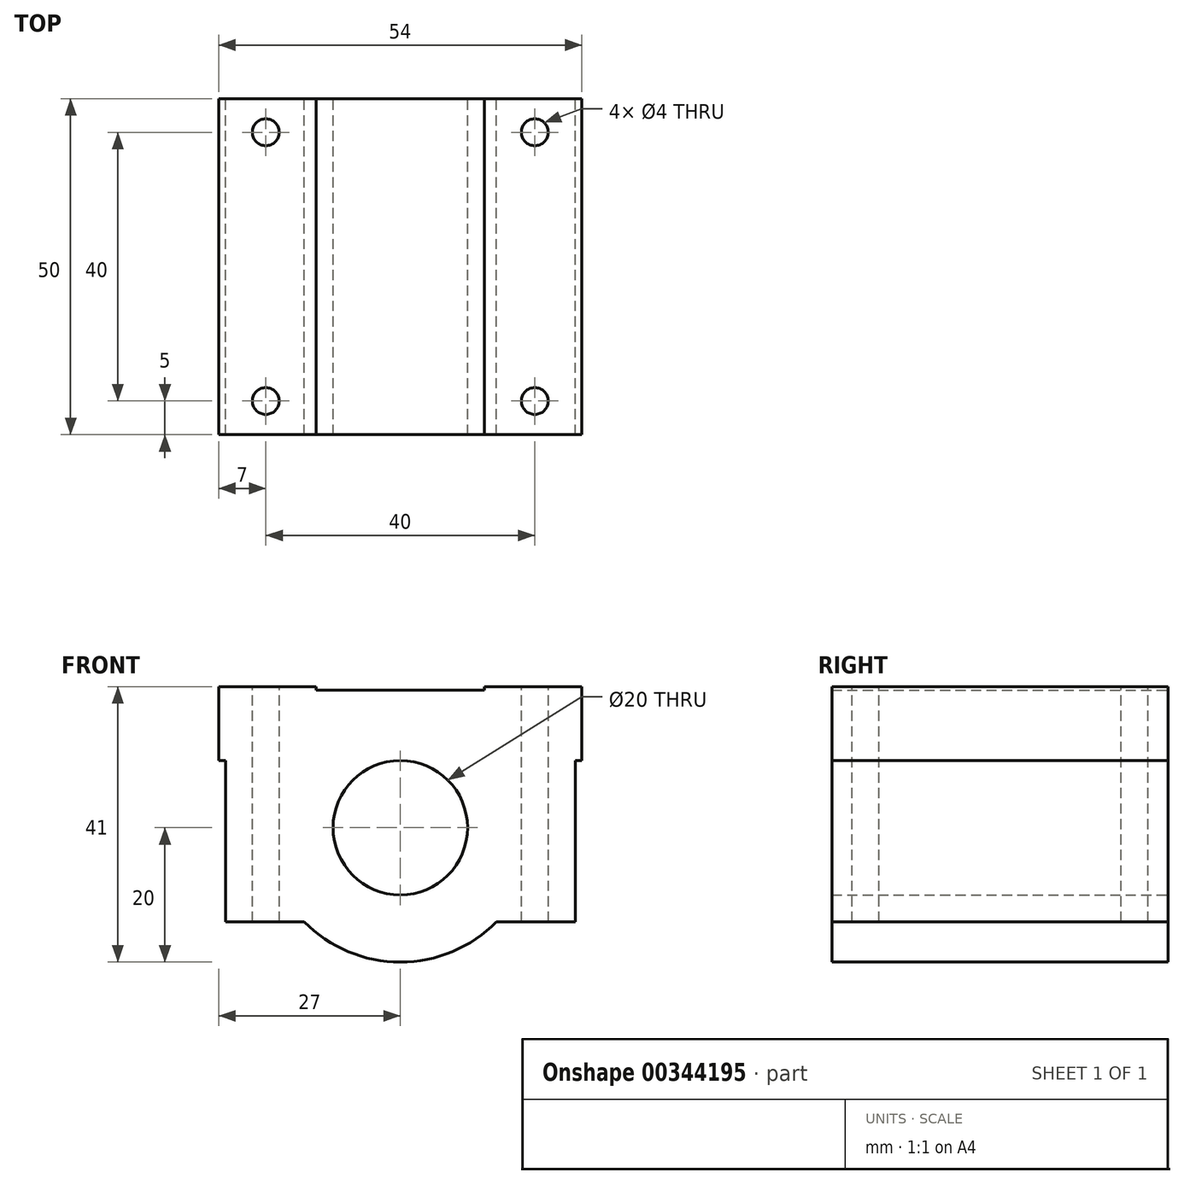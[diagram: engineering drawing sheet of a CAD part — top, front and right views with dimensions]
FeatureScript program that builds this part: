
annotation { "Feature Type Name" : "Feature", "Feature Type Description" : "" }
export const myFeature = defineFeature(function(context is Context, id is Id, definition is map)
    precondition{}
    {
        {
            var Q0;
            Q0=qCreatedBy(makeId("Front.planeOp"),FACE);
            var sketch = newSketch(context, id + "F0", { "sketchPlane" : qUnion([Q0])});
            skLineSegment(sketch, "E0.bottom", {"start": v(26, -17.5) * mm, "end": v(14.28, -17.5) * mm});
            skLineSegment(sketch, "E0.top", {"start": v(27, 17.5) * mm, "end": v(12.5, 17.5) * mm});
            skLineSegment(sketch, "E0.left", {"start": v(27, 6.5) * mm, "end": v(27, 17.5) * mm});
            skLineSegment(sketch, "E0.right", {"start": v(-27, 6.5) * mm, "end": v(-27, 17.5) * mm});
            skPoint(sketch, "E0.middle", {"position": v(0, 0) * mm});
            skCircle(sketch, "E1", {"center": v(0, -3.5) * mm, "radius": 10 * mm});
            skArc(sketch, "E2", {"start": v(-14.28, -17.5) * mm, "mid": v(0, -23.5) * mm, "end": v(14.28, -17.5) * mm});
            skLineSegment(sketch, "E3.trimOffspring", {"start": v(-14.28, -17.5) * mm, "end": v(-26, -17.5) * mm});
            skLineSegment(sketch, "E4.bottom", {"start": v(-27, 6.5) * mm, "end": v(-26, 6.5) * mm});
            skLineSegment(sketch, "E4.right", {"start": v(-26, 6.5) * mm, "end": v(-26, -17.5) * mm});
            skLineSegment(sketch, "E5.bottom", {"start": v(26, 6.5) * mm, "end": v(27, 6.5) * mm});
            skLineSegment(sketch, "E5.left", {"start": v(26, 6.5) * mm, "end": v(26, -17.5) * mm});
            skPoint(sketch, "E6.orphan", {"position": v(27, -17.5) * mm});
            skPoint(sketch, "E7.orphan", {"position": v(-27, -17.5) * mm});
            skLineSegment(sketch, "E8.bottom", {"start": v(-12.5, 17) * mm, "end": v(12.5, 17) * mm});
            skLineSegment(sketch, "E8.left", {"start": v(-12.5, 17) * mm, "end": v(-12.5, 17.5) * mm});
            skLineSegment(sketch, "E8.right", {"start": v(12.5, 17) * mm, "end": v(12.5, 17.5) * mm});
            skPoint(sketch, "E8.middle", {"position": v(0, 21.82) * mm});
            skPoint(sketch, "E8.top.end.orphan", {"position": v(12.5, 26.64) * mm});
            skPoint(sketch, "E9.orphan", {"position": v(-12.5, 26.64) * mm});
            skLineSegment(sketch, "E10.trimOffspring", {"start": v(-12.5, 17.5) * mm, "end": v(-27, 17.5) * mm});
            skSolve(sketch);
        }
        {
            var Q0;
            Q0 = qSketchRegion(id + "F0", true);
            extrude(context, id + "F1", {"entities" : qUnion([Q0]), "depth" : 50 * mm});
        }
        {
            var Q0;
            Q0=makeQuery(id+"F1.opExtrude","SWEPT_FACE",FACE,{"disambiguationData":[OSD([sQuery(id+"F0.wireOp",EDGE,"E0.top")])]});
            var sketch = newSketch(context, id + "F2", { "sketchPlane" : qUnion([Q0])});
            skLineSegment(sketch, "E11", {"start": v(0, -49.66) * mm, "end": v(0, -5.4) * mm, "construction": true});
            skLineSegment(sketch, "E12", {"start": v(27, -25) * mm, "end": v(-26, -25) * mm, "construction": true});
            skPoint(sketch, "E12.endSnap0", {"position": v(27, -25) * mm});
            skLineSegment(sketch, "E13.bottom", {"start": v(-20, -5) * mm, "end": v(20, -5) * mm, "construction": true});
            skLineSegment(sketch, "E13.top", {"start": v(-20, -45) * mm, "end": v(20, -45) * mm, "construction": true});
            skLineSegment(sketch, "E13.left", {"start": v(-20, -5) * mm, "end": v(-20, -45) * mm, "construction": true});
            skLineSegment(sketch, "E13.right", {"start": v(20, -5) * mm, "end": v(20, -45) * mm, "construction": true});
            skPoint(sketch, "E13.middle", {"position": v(0, -25) * mm});
            skCircle(sketch, "E14", {"center": v(20, -45) * mm, "radius": 2 * mm});
            skCircle(sketch, "E15", {"center": v(-20, -45) * mm, "radius": 2 * mm});
            skCircle(sketch, "E16", {"center": v(-20, -5) * mm, "radius": 2 * mm});
            skCircle(sketch, "E17", {"center": v(20, -5) * mm, "radius": 2 * mm});
            skSolve(sketch);
        }
        {
            var Q0;
            Q0 = qSketchRegion(id + "F2", true);
            extrude(context, id + "F3", {"entities" : qUnion([Q0]), "operationType" : NewBodyOperationType.REMOVE, "endBound" : BoundingType.THROUGH_ALL, "oppositeDirection" : true, "depth" : 25 * mm});
        }
    });
